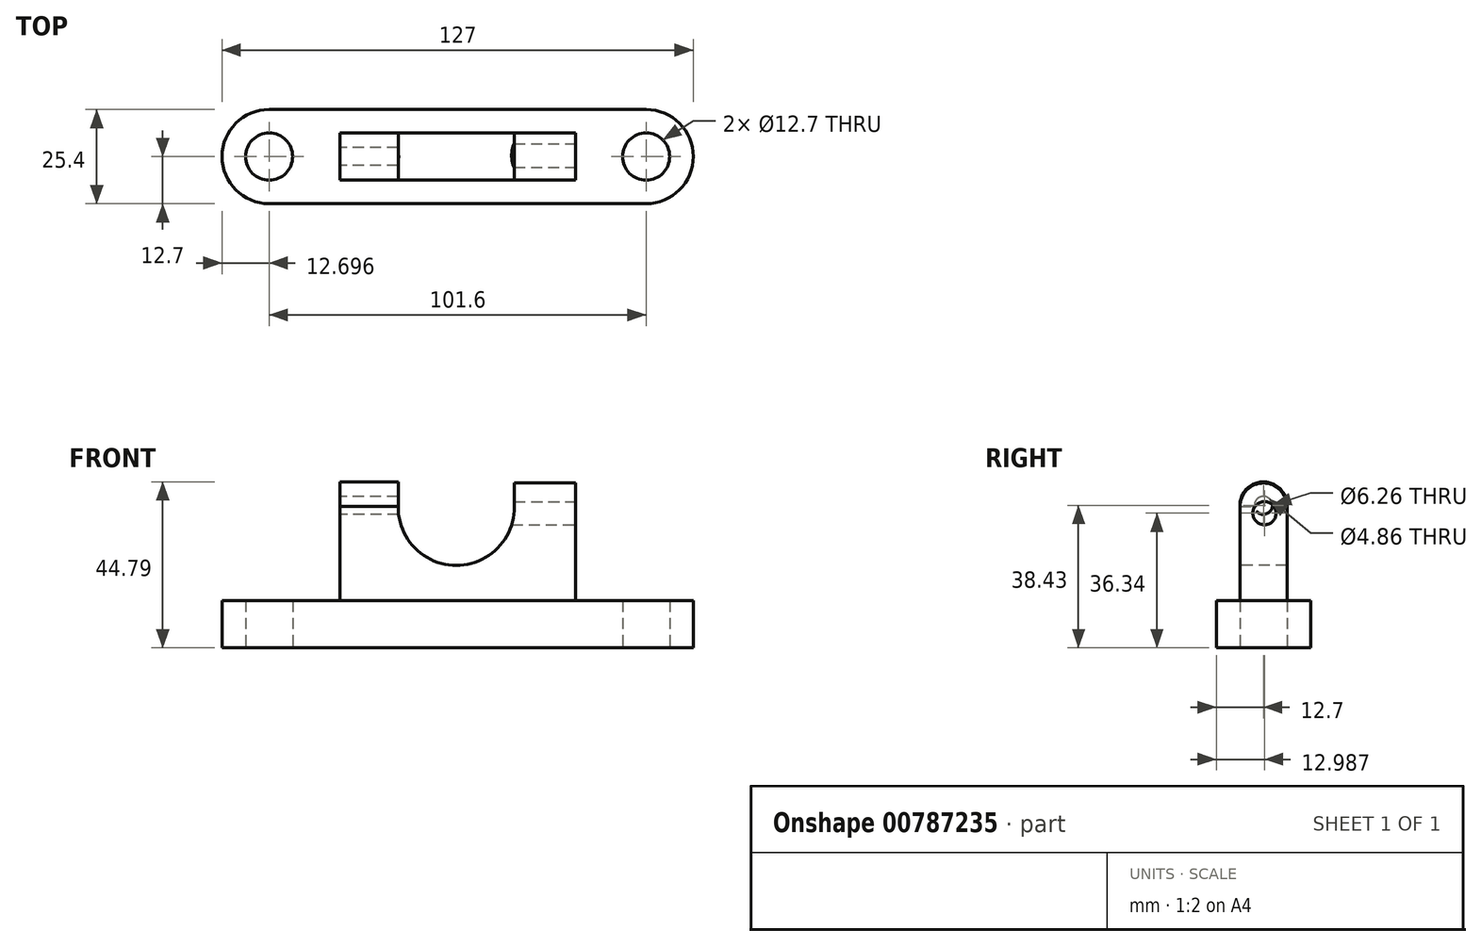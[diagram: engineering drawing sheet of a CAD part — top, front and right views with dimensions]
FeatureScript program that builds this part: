
annotation { "Feature Type Name" : "Feature", "Feature Type Description" : "" }
export const myFeature = defineFeature(function(context is Context, id is Id, definition is map)
    precondition{}
    {
        {
            var Q0;
            Q0=qCreatedBy(makeId("Top.planeOp"),FACE);
            var sketch = newSketch(context, id + "F0", { "sketchPlane" : qUnion([Q0])});
            skLineSegment(sketch, "E0", {"start": v(-66.07, 25.4) * mm, "end": v(35.53, 25.4) * mm});
            skLineSegment(sketch, "E1", {"start": v(35.53, 25.4) * mm, "end": v(35.53, 0) * mm});
            skLineSegment(sketch, "E2", {"start": v(35.53, 0) * mm, "end": v(-66.07, 0) * mm});
            skLineSegment(sketch, "E3", {"start": v(-66.07, 0) * mm, "end": v(-66.07, 25.4) * mm});
            skArc(sketch, "E4", {"start": v(35.53, 0) * mm, "mid": v(48.23, 12.7) * mm, "end": v(35.53, 25.4) * mm});
            skArc(sketch, "E5", {"start": v(-66.07, 25.4) * mm, "mid": v(-78.77, 12.7) * mm, "end": v(-66.07, 0) * mm});
            skLineSegment(sketch, "E6", {"start": v(-47.02, 12.7) * mm, "end": v(-47.02, 6.35) * mm});
            skLineSegment(sketch, "E7", {"start": v(-47.02, 12.7) * mm, "end": v(-47.02, 19.05) * mm});
            skLineSegment(sketch, "E8", {"start": v(-47.02, 19.05) * mm, "end": v(16.48, 19.05) * mm});
            skLineSegment(sketch, "E9", {"start": v(-47.02, 6.35) * mm, "end": v(16.48, 6.35) * mm});
            skLineSegment(sketch, "E10", {"start": v(16.48, 19.05) * mm, "end": v(16.48, 6.35) * mm});
            skCircle(sketch, "E11", {"center": v(-66.07, 12.7) * mm, "radius": 6.35 * mm});
            skCircle(sketch, "E12", {"center": v(35.53, 12.7) * mm, "radius": 6.35 * mm});
            skSolve(sketch);
        }
        {
            var Q0;
            Q0 = qSketchRegion(id + "F0", true);
            var Q1;
            Q1=makeQuery(id+"F0.imprint","IMPRINT",FACE,{"disambiguationData":[TD([[makeQuery(id+"F0.imprint","IMPRINT",EDGE,{"derivedFrom":sQuery(id+"F0.wireOp",EDGE,"E6")}),1.0]])]});
            extrude(context, id + "F1", {"entities" : qUnion([Q0, Q1]), "depth" : 12.7 * mm, "offsetDistance" : 25.4 * mm});
        }
        {
            var Q0;
            Q0=makeQuery(id+"F1.opExtrude","CAP_FACE",FACE,{"disambiguationData":[OSD([sQuery(id+"F0.wireOp",EDGE,"E0"),sQuery(id+"F0.wireOp",EDGE,"E2"),sQuery(id+"F0.wireOp",EDGE,"E4"),sQuery(id+"F0.wireOp",EDGE,"E5"),sQuery(id+"F0.wireOp",EDGE,"E11"),sQuery(id+"F0.wireOp",EDGE,"E12")])],"isStart":false});
            var sketch = newSketch(context, id + "F2", { "sketchPlane" : qUnion([Q0])});
            skPoint(sketch, "E13.endSnap0", {"position": v(-15.27, 0) * mm});
            skLineSegment(sketch, "E14", {"start": v(16.48, 6.35) * mm, "end": v(-47.02, 6.35) * mm});
            skLineSegment(sketch, "E15", {"start": v(-47.02, 19.05) * mm, "end": v(16.48, 19.05) * mm});
            skLineSegment(sketch, "E16", {"start": v(-47.02, 6.35) * mm, "end": v(-47.02, 19.05) * mm});
            skLineSegment(sketch, "E17", {"start": v(16.48, 19.05) * mm, "end": v(16.48, 6.35) * mm});
            skSolve(sketch);
        }
        {
            var Q0;
            Q0=makeQuery(id+"F2.imprint","IMPRINT",FACE,{"disambiguationData":[TD([[makeQuery(id+"F2.imprint","IMPRINT",EDGE,{"derivedFrom":sQuery(id+"F2.wireOp",EDGE,"E14")}),-1.0]])]});
            extrude(context, id + "F3", {"entities" : qUnion([Q0]), "operationType" : NewBodyOperationType.ADD, "depth" : 25.4 * mm, "offsetDistance" : 25.4 * mm});
        }
        {
            var Q0;
            Q0=makeQuery(id+"F3.opExtrude","SWEPT_FACE",FACE,{"disambiguationData":[OSD([sQuery(id+"F2.wireOp",EDGE,"E14")])]});
            var sketch = newSketch(context, id + "F4", { "sketchPlane" : qUnion([Q0])});
            skArc(sketch, "E18", {"start": v(-31.3, 38.1) * mm, "mid": v(-15.65, 22.24) * mm, "end": v(0, 38.1) * mm});
            skSolve(sketch);
        }
        {
            var Q0;
            {var subQ0=sQuery(id+"F4.wireOp",EDGE,"E18");Q0=makeQuery(id+"F4.imprint","IMPRINT",FACE,{"disambiguationData":[TD([[makeQuery(id+"F4.imprint","IMPRINT",EDGE,{"derivedFrom":subQ0}),1.0]])]});}
            extrude(context, id + "F5", {"entities" : qUnion([Q0]), "operationType" : NewBodyOperationType.REMOVE, "oppositeDirection" : true, "depth" : 25.4 * mm, "offsetDistance" : 25.4 * mm});
        }
        {
            var Q0;
            Q0=makeQuery(id+"F3.opExtrude","SWEPT_FACE",FACE,{"disambiguationData":[OSD([sQuery(id+"F2.wireOp",EDGE,"E17")])]});
            var sketch = newSketch(context, id + "F6", { "sketchPlane" : qUnion([Q0])});
            skArc(sketch, "E19", {"start": v(19.05, 38.1) * mm, "mid": v(12.7, 44.45) * mm, "end": v(6.35, 38.1) * mm});
            skSolve(sketch);
        }
        {
            var Q0;
            Q0=makeQuery(id+"F3.opExtrude","SWEPT_FACE",FACE,{"disambiguationData":[OSD([sQuery(id+"F2.wireOp",EDGE,"E16")])]});
            var sketch = newSketch(context, id + "F7", { "sketchPlane" : qUnion([Q0])});
            skArc(sketch, "E20", {"start": v(-6.35, 38.1) * mm, "mid": v(-12.7, 44.79) * mm, "end": v(-19.05, 38.1) * mm});
            skSolve(sketch);
        }
        {
            var Q0;
            Q0=makeQuery(id+"F7.imprint","IMPRINT",FACE,{"disambiguationData":[TD([[makeQuery(id+"F7.imprint","IMPRINT",EDGE,{"derivedFrom":sQuery(id+"F7.wireOp",EDGE,"E20")}),1.0]])]});
            extrude(context, id + "F8", {"entities" : qUnion([Q0]), "operationType" : NewBodyOperationType.ADD, "depth" : -15.72 * mm, "offsetDistance" : 25.4 * mm});
        }
        {
            var Q0;
            Q0=makeQuery(id+"F6.imprint","IMPRINT",FACE,{"disambiguationData":[TD([[makeQuery(id+"F6.imprint","IMPRINT",EDGE,{"derivedFrom":sQuery(id+"F6.wireOp",EDGE,"E19")}),1.0]])]});
            extrude(context, id + "F9", {"entities" : qUnion([Q0]), "operationType" : NewBodyOperationType.ADD, "depth" : -16.5 * mm, "offsetDistance" : 25.4 * mm});
        }
        {
            var Q0;
            {var subQ0=sQuery(id+"F2.wireOp",EDGE,"E16");Q0=makeQuery(id+"F8.boolean.opBoolean","MERGE",FACE,{"derivedFrom":[makeQuery(id+"F3.opExtrude","SWEPT_FACE",FACE,{"disambiguationData":[OSD([subQ0])]}),makeQuery(id+"F8.opExtrude","CAP_FACE",FACE,{"disambiguationData":[OSD([subQ0,sQuery(id+"F7.wireOp",EDGE,"E20")])],"isStart":true})]});}
            var sketch = newSketch(context, id + "F10", { "sketchPlane" : qUnion([Q0])});
            skCircle(sketch, "E21", {"center": v(-12.7, 38.43) * mm, "radius": 2.43 * mm});
            skSolve(sketch);
        }
        {
            var Q0;
            {var subQ0=sQuery(id+"F2.wireOp",EDGE,"E17");Q0=makeQuery(id+"F9.boolean.opBoolean","MERGE",FACE,{"derivedFrom":[makeQuery(id+"F3.opExtrude","SWEPT_FACE",FACE,{"disambiguationData":[OSD([subQ0])]}),makeQuery(id+"F9.opExtrude","CAP_FACE",FACE,{"disambiguationData":[OSD([subQ0,sQuery(id+"F6.wireOp",EDGE,"E19")])],"isStart":true})]});}
            var sketch = newSketch(context, id + "F11", { "sketchPlane" : qUnion([Q0])});
            skCircle(sketch, "E22", {"center": v(12.99, 36.34) * mm, "radius": 3.13 * mm});
            skSolve(sketch);
        }
        {
            var Q0;
            Q0=makeQuery(id+"F11.imprint","IMPRINT",FACE,{"disambiguationData":[TD([[makeQuery(id+"F11.imprint","IMPRINT",EDGE,{"derivedFrom":sQuery(id+"F11.wireOp",EDGE,"E22")}),1.0]])]});
            extrude(context, id + "F12", {"entities" : qUnion([Q0]), "operationType" : NewBodyOperationType.REMOVE, "depth" : -25.4 * mm, "offsetDistance" : 25.4 * mm});
        }
        {
            var Q0;
            Q0=makeQuery(id+"F10.imprint","IMPRINT",FACE,{"disambiguationData":[TD([[makeQuery(id+"F10.imprint","IMPRINT",EDGE,{"derivedFrom":sQuery(id+"F10.wireOp",EDGE,"E21")}),1.0]])]});
            extrude(context, id + "F13", {"entities" : qUnion([Q0]), "operationType" : NewBodyOperationType.REMOVE, "oppositeDirection" : true, "depth" : 25.4 * mm, "offsetDistance" : 25.4 * mm});
        }
    });
